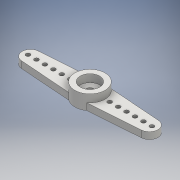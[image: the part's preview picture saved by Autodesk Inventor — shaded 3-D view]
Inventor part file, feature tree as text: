
AUTODESK INVENTOR PART (.ipt)
format: ipt  version: 2016 (Build 200138000, 138)  size: 169,472 bytes
history: native  units: mm
features: extrude x5, sketch x5, other x1
ambient origin geometry x8: Origin, YZ Plane, XZ Plane, XY Plane, X Axis, Y Axis, Z Axis, Center Point
bodies: Body1 (feature_tree)
feature tree (11):
  other  "Sólido1"
  extrude  "Extrusión1"  Depth=1.6mm TaperAngle=0.0deg
  extrude  "Extrusión2"  Depth=0.63mm TaperAngle=0.0deg
  extrude  "Extrusión3"  Depth=1.83mm TaperAngle=0.0deg
  extrude  "Extrusión4"  [1 undecoded]
  extrude  "Extrusión5"  [1 undecoded]
  sketch  "Boceto1"  dims[d8=60.0mm d10=2.0mm d11=10.0mm d13=10.0mm d18=1.6mm d19=0.0mm]
  sketch  "Boceto2"  dims[d21=3.43mm d22=0.0mm d24=0.63mm d25=0.0mm]
  sketch  "Boceto3"  dims[d27=0.63mm d28=0.0mm d30=1.83mm d31=0.0mm]
  sketch  "Boceto4"
  sketch  "Boceto5"
note: 2 required parameter values undecoded (feature->parameter linkage not recoverable at this tier; creation-order binding heuristic only, values carry confidence <= 0.55)
